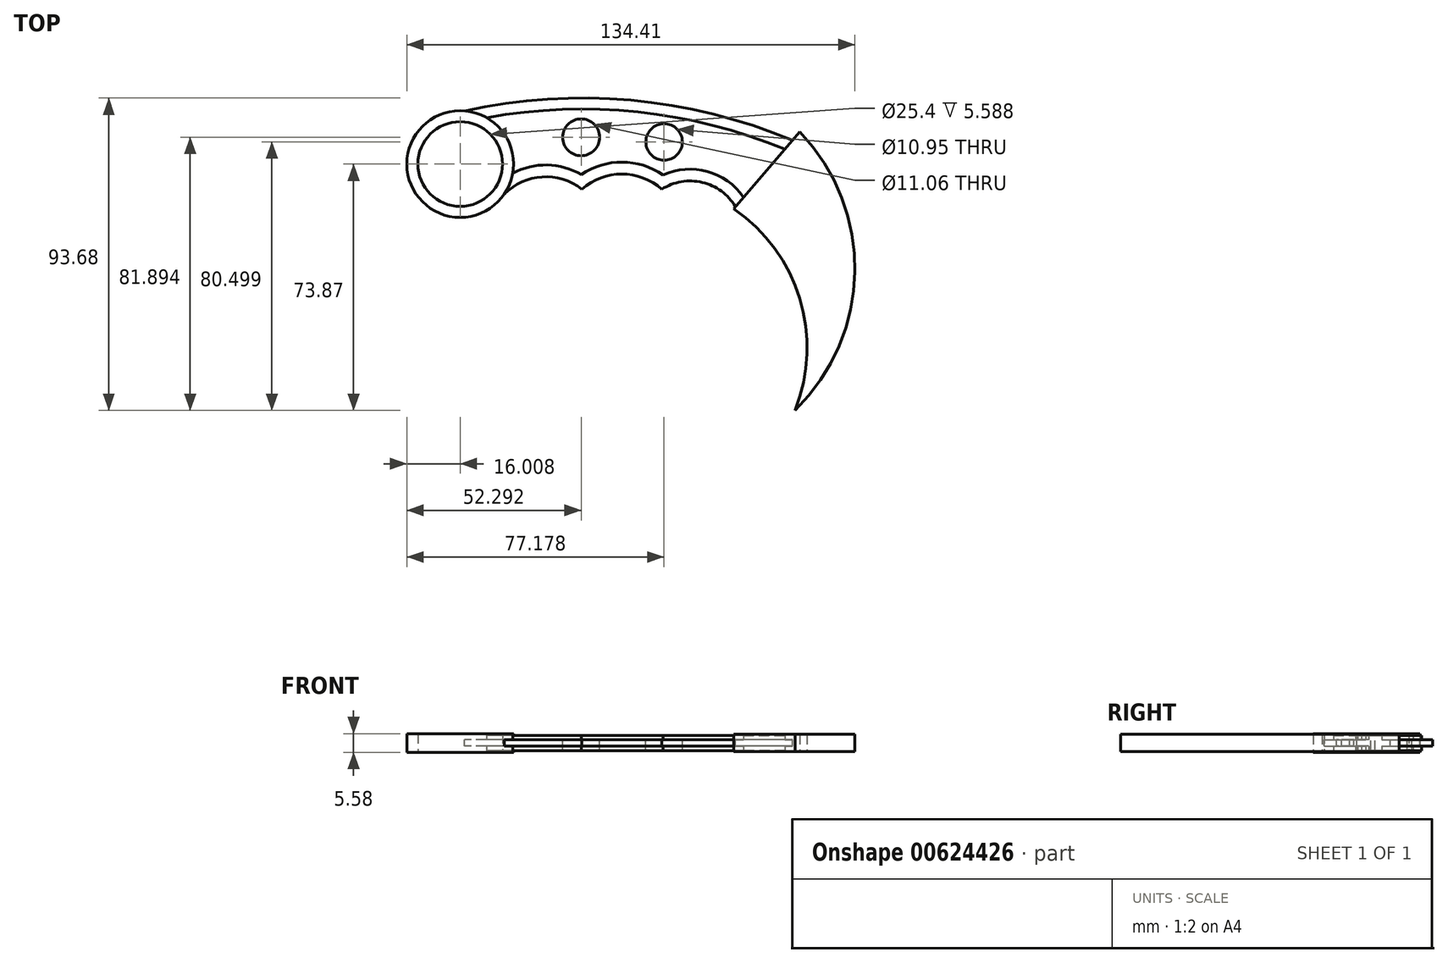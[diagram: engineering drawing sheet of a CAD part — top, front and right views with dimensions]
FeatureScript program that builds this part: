
annotation { "Feature Type Name" : "Feature", "Feature Type Description" : "" }
export const myFeature = defineFeature(function(context is Context, id is Id, definition is map)
    precondition{}
    {
        {
            var Q0;
            Q0=qCreatedBy(makeId("Top.planeOp"),FACE);
            var sketch = newSketch(context, id + "F0", { "sketchPlane" : qUnion([Q0])});
            skCircle(sketch, "E0", {"center": v(-55.47, 0) * mm, "radius": 12.7 * mm});
            skCircle(sketch, "E1", {"center": v(-55.47, 0) * mm, "radius": 16 * mm});
            skSolve(sketch);
        }
        {
            var Q0;
            Q0 = qSketchRegion(id + "F0", true);
            extrude(context, id + "F1", {"entities" : qUnion([Q0]), "endBound" : BoundingType.SYMMETRIC, "depth" : 5.6 * mm, "offsetDistance" : 25.4 * mm});
        }
        {
            var Q0;
            Q0=qCreatedBy(makeId("Top.planeOp"),FACE);
            var sketch = newSketch(context, id + "F2", { "sketchPlane" : qUnion([Q0])});
            skArc(sketch, "E2", {"start": v(44.77, 6.86) * mm, "mid": v(-4.06, 19.13) * mm, "end": v(-54.3, 15.93) * mm});
            skArc(sketch, "E3", {"start": v(-18.96, -7.56) * mm, "mid": v(-32.49, -4.05) * mm, "end": v(-44.3, -11.51) * mm});
            skArc(sketch, "E4", {"start": v(5, -7.56) * mm, "mid": v(-6.98, -2.97) * mm, "end": v(-18.96, -7.56) * mm});
            skArc(sketch, "E5", {"start": v(27.33, -13.14) * mm, "mid": v(17.36, -5.55) * mm, "end": v(5, -7.56) * mm});
            skLineSegment(sketch, "E6", {"start": v(27.33, -13.14) * mm, "end": v(44.77, 6.86) * mm});
            skArc(sketch, "E7", {"start": v(-44.3, -11.51) * mm, "mid": v(-40.57, 5.4) * mm, "end": v(-54.3, 15.93) * mm});
            skSolve(sketch);
        }
        {
            var Q0;
            {var subQ4=sQuery(id+"F2.wireOp",EDGE,"E2");Q0=makeQuery(id+"F2.imprint","IMPRINT",FACE,{"disambiguationData":[TD([[makeQuery(id+"F2.imprint","IMPRINT",EDGE,{"derivedFrom":subQ4}),1.0]])]});}
            var sketch = newSketch(context, id + "F3", { "sketchPlane" : qUnion([Q0])});
            skArc(sketch, "E8.0", {"start": v(-19.11, -3.17) * mm, "mid": v(-32.2, -0.42) * mm, "end": v(-44.33, -6.08) * mm});
            skArc(sketch, "E8.1", {"start": v(5.37, -3.32) * mm, "mid": v(-6.85, 0.59) * mm, "end": v(-19.11, -3.17) * mm});
            skArc(sketch, "E8.2", {"start": v(29.72, -10.23) * mm, "mid": v(18.82, -2.26) * mm, "end": v(5.37, -3.32) * mm});
            skArc(sketch, "E9.0", {"start": v(42.4, 4.28) * mm, "mid": v(-4.95, 15.9) * mm, "end": v(-53.6, 12.7) * mm});
            skArc(sketch, "E10", {"start": v(-44.33, -6.08) * mm, "mid": v(-44.09, 5.72) * mm, "end": v(-53.6, 12.7) * mm});
            skLineSegment(sketch, "E11", {"start": v(29.72, -10.23) * mm, "end": v(42.4, 4.28) * mm});
            skSolve(sketch);
        }
        {
            var Q0;
            {var subQ7=sQuery(id+"F3.wireOp",EDGE,"E8.1");Q0=makeQuery(id+"F3.imprint","IMPRINT",FACE,{"disambiguationData":[TD([[makeQuery(id+"F3.imprint","IMPRINT",EDGE,{"derivedFrom":subQ7}),-1.0]])]});}
            extrude(context, id + "F4", {"entities" : qUnion([Q0]), "operationType" : NewBodyOperationType.ADD, "endBound" : BoundingType.SYMMETRIC, "depth" : 4.57 * mm, "offsetDistance" : 25.4 * mm});
        }
        {
            var Q0;
            {var subQ4=sQuery(id+"F2.wireOp",EDGE,"E2");Q0=makeQuery(id+"F2.imprint","IMPRINT",FACE,{"disambiguationData":[TD([[makeQuery(id+"F2.imprint","IMPRINT",EDGE,{"derivedFrom":subQ4}),1.0]])]});}
            extrude(context, id + "F5", {"entities" : qUnion([Q0]), "operationType" : NewBodyOperationType.ADD, "endBound" : BoundingType.SYMMETRIC, "oppositeDirection" : true, "depth" : 1.88 * mm, "offsetDistance" : 25.4 * mm});
        }
        {
            var Q0;
            Q0=qCreatedBy(makeId("Top.planeOp"),FACE);
            var sketch = newSketch(context, id + "F6", { "sketchPlane" : qUnion([Q0])});
            skLineSegment(sketch, "E12", {"start": v(46.45, 9.73) * mm, "end": v(26.6, -13.4) * mm});
            skArc(sketch, "E13", {"start": v(44.95, -73.87) * mm, "mid": v(46.42, -40.4) * mm, "end": v(26.6, -13.4) * mm});
            skArc(sketch, "E14", {"start": v(44.95, -73.87) * mm, "mid": v(62.92, -32.38) * mm, "end": v(46.45, 9.73) * mm});
            skSolve(sketch);
        }
        {
            var Q0;
            Q0=makeQuery(id+"F6.imprint","IMPRINT",FACE,{"disambiguationData":[TD([[makeQuery(id+"F6.imprint","IMPRINT",EDGE,{"derivedFrom":sQuery(id+"F6.wireOp",EDGE,"E12")}),1.0]])]});
            extrude(context, id + "F7", {"entities" : qUnion([Q0]), "operationType" : NewBodyOperationType.ADD, "endBound" : BoundingType.SYMMETRIC, "depth" : 5.23 * mm, "offsetDistance" : 25.4 * mm});
        }
        {
            var Q0;
            Q0=qCreatedBy(makeId("Top.planeOp"),FACE);
            var sketch = newSketch(context, id + "F8", { "sketchPlane" : qUnion([Q0])});
            skCircle(sketch, "E15", {"center": v(-19.19, 8.02) * mm, "radius": 5.53 * mm});
            skCircle(sketch, "E16", {"center": v(5.7, 6.63) * mm, "radius": 5.47 * mm});
            skSolve(sketch);
        }
        {
            var Q0;
            Q0 = qSketchRegion(id + "F8", true);
            extrude(context, id + "F9", {"entities" : qUnion([Q0]), "operationType" : NewBodyOperationType.REMOVE, "endBound" : BoundingType.THROUGH_ALL, "oppositeDirection" : true, "depth" : 25.4 * mm, "offsetDistance" : 25.4 * mm});
        }
        {
            var Q0;
            Q0=makeQuery(id+"F9.boolean.opBoolean","COPY",FACE,{"derivedFrom":makeQuery(id+"F9.opExtrude","CAP_FACE",FACE,{"disambiguationData":[OSD([sQuery(id+"F8.wireOp",EDGE,"E15")])],"isStart":true})});
            var sketch = newSketch(context, id + "F10", { "sketchPlane" : qUnion([Q0])});
            skCircle(sketch, "E17.0", {"center": v(-19.19, -8.02) * mm, "radius": 5.53 * mm});
            skSolve(sketch);
        }
        {
            var Q0;
            Q0 = qSketchRegion(id + "F10", true);
            extrude(context, id + "F11", {"entities" : qUnion([Q0]), "operationType" : NewBodyOperationType.REMOVE, "endBound" : BoundingType.THROUGH_ALL, "oppositeDirection" : true, "depth" : 25.4 * mm, "offsetDistance" : 25.4 * mm});
        }
        {
            var Q0;
            Q0=makeQuery(id+"F9.boolean.opBoolean","COPY",FACE,{"derivedFrom":makeQuery(id+"F9.opExtrude","CAP_FACE",FACE,{"disambiguationData":[OSD([sQuery(id+"F8.wireOp",EDGE,"E16")])],"isStart":true})});
            var sketch = newSketch(context, id + "F12", { "sketchPlane" : qUnion([Q0])});
            skCircle(sketch, "E18.0", {"center": v(5.7, -6.63) * mm, "radius": 5.47 * mm});
            skSolve(sketch);
        }
        {
            var Q0;
            Q0 = qSketchRegion(id + "F12", true);
            extrude(context, id + "F13", {"entities" : qUnion([Q0]), "operationType" : NewBodyOperationType.REMOVE, "endBound" : BoundingType.THROUGH_ALL, "oppositeDirection" : true, "depth" : 25.4 * mm, "offsetDistance" : 25.4 * mm});
        }
    });
